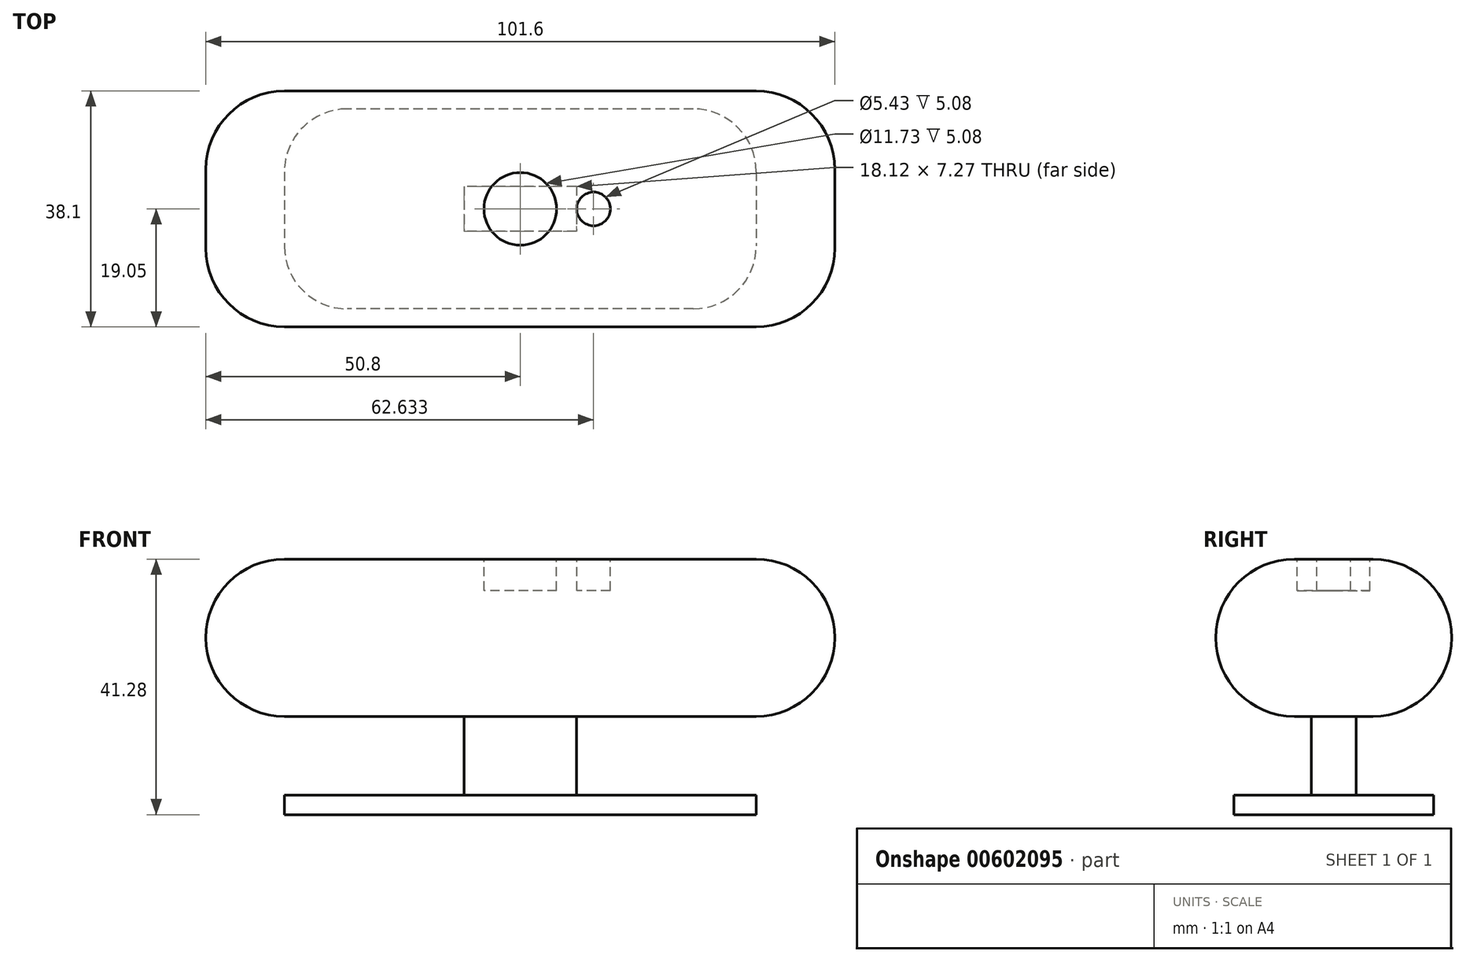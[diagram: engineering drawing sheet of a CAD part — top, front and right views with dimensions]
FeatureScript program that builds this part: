
annotation { "Feature Type Name" : "Feature", "Feature Type Description" : "" }
export const myFeature = defineFeature(function(context is Context, id is Id, definition is map)
    precondition{}
    {
        {
            var Q0;
            Q0=qCreatedBy(makeId("Top.planeOp"),FACE);
            var sketch = newSketch(context, id + "F0", { "sketchPlane" : qUnion([Q0])});
            skLineSegment(sketch, "E0.bottom", {"start": v(38.1, 16.15) * mm, "end": v(-38.1, 16.15) * mm});
            skLineSegment(sketch, "E0.top", {"start": v(38.1, -16.15) * mm, "end": v(-38.1, -16.15) * mm});
            skLineSegment(sketch, "E0.left", {"start": v(38.1, 16.15) * mm, "end": v(38.1, -16.15) * mm});
            skLineSegment(sketch, "E0.right", {"start": v(-38.1, 16.15) * mm, "end": v(-38.1, -16.15) * mm});
            skPoint(sketch, "E0.middle", {"position": v(0, 0) * mm});
            skSolve(sketch);
        }
        {
            var Q0;
            Q0=makeQuery(id+"F0.imprint","IMPRINT",FACE,{"disambiguationData":[TD([[makeQuery(id+"F0.imprint","IMPRINT",EDGE,{"derivedFrom":sQuery(id+"F0.wireOp",EDGE,"E0.bottom")}),1.0]])]});
            extrude(context, id + "F1", {"entities" : qUnion([Q0]), "depth" : 3.17 * mm, "offsetDistance" : 25.4 * mm});
        }
        {
            var Q0;
            Q0=makeQuery(id+"F1.opExtrude","SWEPT_EDGE",EDGE,{"disambiguationData":[OSD([sQuery(id+"F0.wireOp",EDGE,"E0.top"),sQuery(id+"F0.wireOp",EDGE,"E0.right")])]});
            var Q1;
            Q1=makeQuery(id+"F1.opExtrude","SWEPT_EDGE",EDGE,{"disambiguationData":[OSD([sQuery(id+"F0.wireOp",EDGE,"E0.top"),sQuery(id+"F0.wireOp",EDGE,"E0.left")])]});
            var Q2;
            Q2=makeQuery(id+"F1.opExtrude","SWEPT_EDGE",EDGE,{"disambiguationData":[OSD([sQuery(id+"F0.wireOp",EDGE,"E0.bottom"),sQuery(id+"F0.wireOp",EDGE,"E0.left")])]});
            var Q3;
            Q3=makeQuery(id+"F1.opExtrude","SWEPT_EDGE",EDGE,{"disambiguationData":[OSD([sQuery(id+"F0.wireOp",EDGE,"E0.bottom"),sQuery(id+"F0.wireOp",EDGE,"E0.right")])]});
            fillet(context, id + "F2", {"entities" : qUnion([Q0, Q1, Q2, Q3]), "radius" : 10.16 * mm, "tangentPropagation" : true, "allowEdgeOverflow" : false});
        }
        {
            var Q0;
            Q0=makeQuery(id+"F1.opExtrude","CAP_FACE",FACE,{"disambiguationData":[OSD([sQuery(id+"F0.wireOp",EDGE,"E0.bottom"),sQuery(id+"F0.wireOp",EDGE,"E0.top"),sQuery(id+"F0.wireOp",EDGE,"E0.left"),sQuery(id+"F0.wireOp",EDGE,"E0.right")])],"isStart":false});
            var sketch = newSketch(context, id + "F3", { "sketchPlane" : qUnion([Q0])});
            skLineSegment(sketch, "E1.bottom", {"start": v(9.06, 3.64) * mm, "end": v(-9.06, 3.64) * mm});
            skLineSegment(sketch, "E1.top", {"start": v(9.06, -3.64) * mm, "end": v(-9.06, -3.64) * mm});
            skLineSegment(sketch, "E1.left", {"start": v(9.06, 3.64) * mm, "end": v(9.06, -3.64) * mm});
            skLineSegment(sketch, "E1.right", {"start": v(-9.06, 3.64) * mm, "end": v(-9.06, -3.64) * mm});
            skPoint(sketch, "E1.middle", {"position": v(0, 0) * mm});
            skSolve(sketch);
        }
        {
            var Q0;
            Q0=makeQuery(id+"F3.imprint","IMPRINT",FACE,{"disambiguationData":[TD([[makeQuery(id+"F3.imprint","IMPRINT",EDGE,{"derivedFrom":sQuery(id+"F3.wireOp",EDGE,"E1.bottom")}),1.0]])]});
            extrude(context, id + "F4", {"entities" : qUnion([Q0]), "operationType" : NewBodyOperationType.ADD, "depth" : 12.7 * mm, "offsetDistance" : 25.4 * mm});
        }
        {
            var Q0;
            Q0=makeQuery(id+"F4.opExtrude","CAP_FACE",FACE,{"disambiguationData":[OSD([sQuery(id+"F3.wireOp",EDGE,"E1.bottom"),sQuery(id+"F3.wireOp",EDGE,"E1.top"),sQuery(id+"F3.wireOp",EDGE,"E1.left"),sQuery(id+"F3.wireOp",EDGE,"E1.right")])],"isStart":false});
            var sketch = newSketch(context, id + "F5", { "sketchPlane" : qUnion([Q0])});
            skLineSegment(sketch, "E2.bottom", {"start": v(50.8, 19.05) * mm, "end": v(-50.8, 19.05) * mm});
            skLineSegment(sketch, "E2.top", {"start": v(50.8, -19.05) * mm, "end": v(-50.8, -19.05) * mm});
            skLineSegment(sketch, "E2.left", {"start": v(50.8, 19.05) * mm, "end": v(50.8, -19.05) * mm});
            skLineSegment(sketch, "E2.right", {"start": v(-50.8, 19.05) * mm, "end": v(-50.8, -19.05) * mm});
            skPoint(sketch, "E2.middle", {"position": v(0, 0) * mm});
            skSolve(sketch);
        }
        {
            var Q0;
            Q0=makeQuery(id+"F5.imprint","IMPRINT",FACE,{"disambiguationData":[TD([[makeQuery(id+"F5.imprint","IMPRINT",EDGE,{"derivedFrom":sQuery(id+"F5.wireOp",EDGE,"E2.bottom")}),1.0]])]});
            var Q1;
            Q1=makeQuery(id+"F5.imprint","IMPRINT",FACE,{"disambiguationData":[TD([[makeQuery(id+"F5.imprint","IMPRINT",EDGE,{"derivedFrom":makeQuery(id+"F4.opExtrude","CAP_EDGE",EDGE,{"disambiguationData":[OSD([sQuery(id+"F3.wireOp",EDGE,"E1.bottom")])],"isStart":false})}),1.0]])]});
            extrude(context, id + "F6", {"entities" : qUnion([Q0, Q1]), "operationType" : NewBodyOperationType.ADD, "depth" : 25.4 * mm, "offsetDistance" : 25.4 * mm});
        }
        {
            var Q0;
            Q0=makeQuery(id+"F6.opExtrude","SWEPT_EDGE",EDGE,{"disambiguationData":[OSD([sQuery(id+"F5.wireOp",EDGE,"E2.top"),sQuery(id+"F5.wireOp",EDGE,"E2.right")])]});
            var Q1;
            Q1=makeQuery(id+"F6.opExtrude","CAP_EDGE",EDGE,{"disambiguationData":[OSD([sQuery(id+"F5.wireOp",EDGE,"E2.top")])],"isStart":false});
            var Q2;
            Q2=makeQuery(id+"F6.opExtrude","CAP_EDGE",EDGE,{"disambiguationData":[OSD([sQuery(id+"F5.wireOp",EDGE,"E2.top")])],"isStart":true});
            var Q3;
            Q3=makeQuery(id+"F6.opExtrude","SWEPT_EDGE",EDGE,{"disambiguationData":[OSD([sQuery(id+"F5.wireOp",EDGE,"E2.top"),sQuery(id+"F5.wireOp",EDGE,"E2.left")])]});
            var Q4;
            Q4=makeQuery(id+"F6.opExtrude","CAP_EDGE",EDGE,{"disambiguationData":[OSD([sQuery(id+"F5.wireOp",EDGE,"E2.left")])],"isStart":false});
            var Q5;
            Q5=makeQuery(id+"F6.opExtrude","CAP_EDGE",EDGE,{"disambiguationData":[OSD([sQuery(id+"F5.wireOp",EDGE,"E2.left")])],"isStart":true});
            var Q6;
            Q6=makeQuery(id+"F6.opExtrude","CAP_EDGE",EDGE,{"disambiguationData":[OSD([sQuery(id+"F5.wireOp",EDGE,"E2.right")])],"isStart":false});
            var Q7;
            Q7=makeQuery(id+"F6.opExtrude","CAP_EDGE",EDGE,{"disambiguationData":[OSD([sQuery(id+"F5.wireOp",EDGE,"E2.right")])],"isStart":true});
            var Q8;
            Q8=makeQuery(id+"F6.opExtrude","CAP_EDGE",EDGE,{"disambiguationData":[OSD([sQuery(id+"F5.wireOp",EDGE,"E2.bottom")])],"isStart":true});
            var Q9;
            Q9=makeQuery(id+"F6.opExtrude","CAP_EDGE",EDGE,{"disambiguationData":[OSD([sQuery(id+"F5.wireOp",EDGE,"E2.bottom")])],"isStart":false});
            var Q10;
            Q10=makeQuery(id+"F6.opExtrude","SWEPT_EDGE",EDGE,{"disambiguationData":[OSD([sQuery(id+"F5.wireOp",EDGE,"E2.bottom"),sQuery(id+"F5.wireOp",EDGE,"E2.left")])]});
            var Q11;
            Q11=makeQuery(id+"F6.opExtrude","SWEPT_EDGE",EDGE,{"disambiguationData":[OSD([sQuery(id+"F5.wireOp",EDGE,"E2.bottom"),sQuery(id+"F5.wireOp",EDGE,"E2.right")])]});
            fillet(context, id + "F7", {"entities" : qUnion([Q0, Q1, Q2, Q3, Q4, Q5, Q6, Q7, Q8, Q9, Q10, Q11]), "radius" : 12.7 * mm, "tangentPropagation" : true, "allowEdgeOverflow" : false});
        }
        {
            var Q0;
            Q0=makeQuery(id+"F6.opExtrude","CAP_FACE",FACE,{"disambiguationData":[OSD([sQuery(id+"F5.wireOp",EDGE,"E2.bottom"),sQuery(id+"F5.wireOp",EDGE,"E2.top"),sQuery(id+"F5.wireOp",EDGE,"E2.left"),sQuery(id+"F5.wireOp",EDGE,"E2.right")])],"isStart":false});
            var sketch = newSketch(context, id + "F8", { "sketchPlane" : qUnion([Q0])});
            skCircle(sketch, "E3", {"center": v(0, 0) * mm, "radius": 5.87 * mm});
            skCircle(sketch, "E4", {"center": v(11.83, 0) * mm, "radius": 2.71 * mm});
            skSolve(sketch);
        }
        {
            var Q0;
            Q0=makeQuery(id+"F8.imprint","IMPRINT",FACE,{"disambiguationData":[TD([[makeQuery(id+"F8.imprint","IMPRINT",EDGE,{"derivedFrom":sQuery(id+"F8.wireOp",EDGE,"E3")}),1.0]])]});
            var Q1;
            Q1=makeQuery(id+"F8.imprint","IMPRINT",FACE,{"disambiguationData":[TD([[makeQuery(id+"F8.imprint","IMPRINT",EDGE,{"derivedFrom":sQuery(id+"F8.wireOp",EDGE,"E4")}),1.0]])]});
            extrude(context, id + "F9", {"entities" : qUnion([Q0, Q1]), "operationType" : NewBodyOperationType.REMOVE, "oppositeDirection" : true, "depth" : 5.08 * mm, "offsetDistance" : 25.4 * mm});
        }
    });
